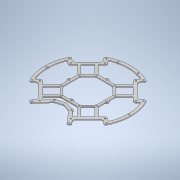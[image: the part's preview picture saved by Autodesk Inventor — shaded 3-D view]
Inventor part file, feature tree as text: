
AUTODESK INVENTOR PART (.ipt)
format: ipt  version: 2020 (Build 240168000, 168)  size: 1,053,696 bytes
history: native  units: mm
features: extrude x9, sketch x6, projected_geometry x5, other x1
ambient origin geometry x8: Origin, YZ Plane, XZ Plane, XY Plane, X Axis, Y Axis, Z Axis, Center Point
bodies: Body1 (feature_tree)
feature tree (21):
  other  "Твердое тело1"
  extrude  "outer"  TaperAngle=45.0deg  [1 undecoded]
  extrude  "inner"  Depth=7.0mm
  sketch  "Эскиз3"
  extrude  "Выдавливание3"  Depth=20.0mm
  extrude  "Выдавливание4"  Depth=7.0mm
  sketch  "Эскиз4"
  extrude  "Выдавливание5"  Depth=3.2mm
  extrude  "Выдавливание6"  Depth=59.0mm
  sketch  "Эскиз5"
  extrude  "Выдавливание7"  Depth=83.0mm
  extrude  "Выдавливание8"  Depth=69.0mm
  extrude  "Выдавливание9"  Depth=55.0mm
  sketch  "Эскиз1"
  sketch  "Эскиз2"
  projected_geometry  "Спроецированная петля1"
  projected_geometry  "Спроецированная петля2"
  projected_geometry  "Спроецированная петля3"
  projected_geometry  "Спроецированная петля4"
  sketch  "Эскиз6"
  projected_geometry  "Спроецированная петля5"
note: 1 required parameter value undecoded (feature->parameter linkage not recoverable at this tier; creation-order binding heuristic only, values carry confidence <= 0.55)
